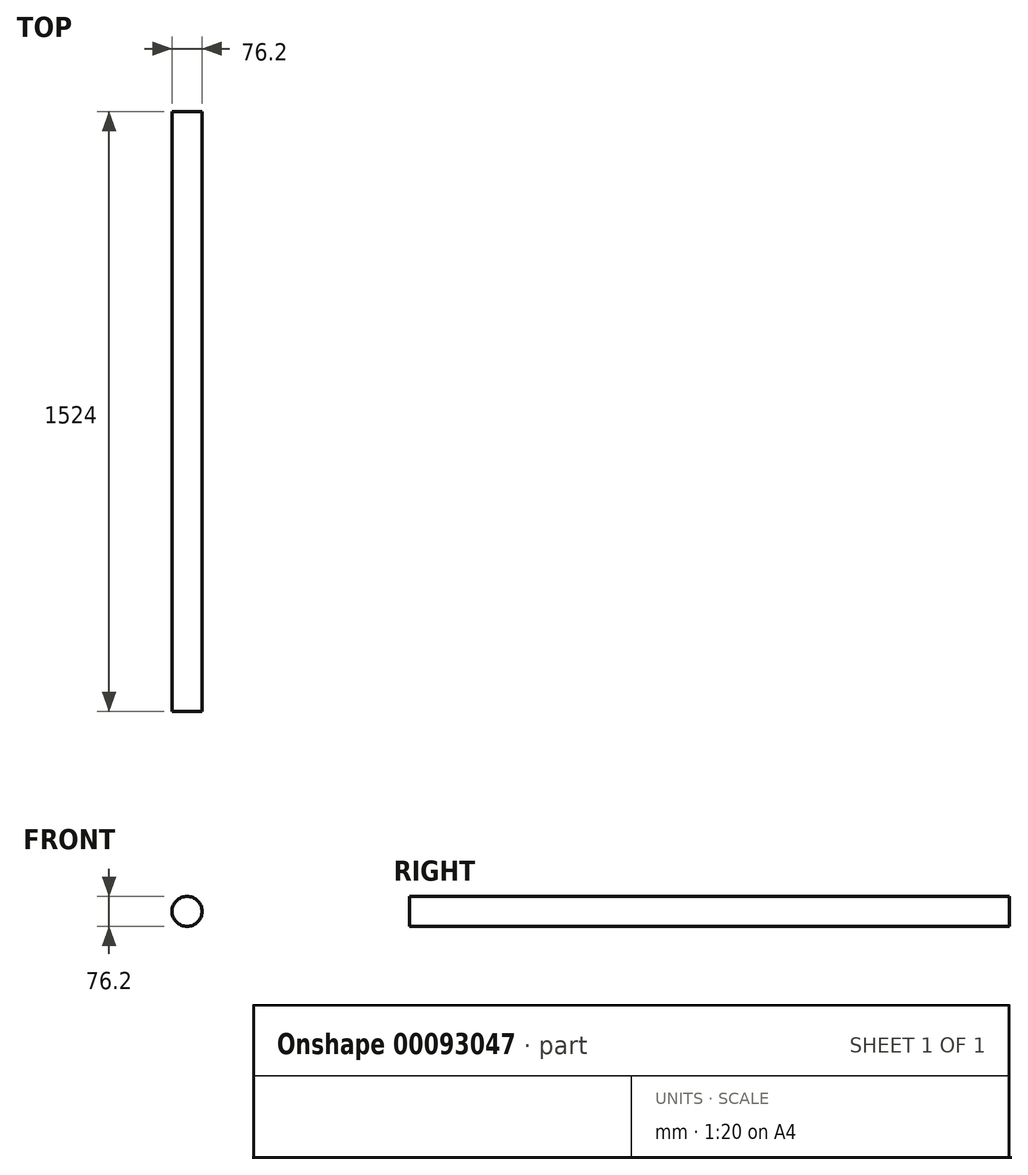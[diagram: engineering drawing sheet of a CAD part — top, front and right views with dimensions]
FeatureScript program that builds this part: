
annotation { "Feature Type Name" : "Feature", "Feature Type Description" : "" }
export const myFeature = defineFeature(function(context is Context, id is Id, definition is map)
    precondition{}
    {
        {
            var Q0;
            Q0=qCreatedBy(makeId("Front.planeOp"),FACE);
            var sketch = newSketch(context, id + "F0", { "sketchPlane" : qUnion([Q0])});
            skCircle(sketch, "E0", {"center": v(0, 0) * mm, "radius": 38.1 * mm});
            skSolve(sketch);
        }
        {
            var Q0;
            Q0=makeQuery(id+"F0.imprint","IMPRINT",FACE,{"disambiguationData":[TD([[makeQuery(id+"F0.imprint","IMPRINT",EDGE,{"derivedFrom":sQuery(id+"F0.wireOp",EDGE,"E0")}),1.0]])]});
            extrude(context, id + "F1", {"entities" : qUnion([Q0]), "depth" : 1524 * mm});
        }
    });
